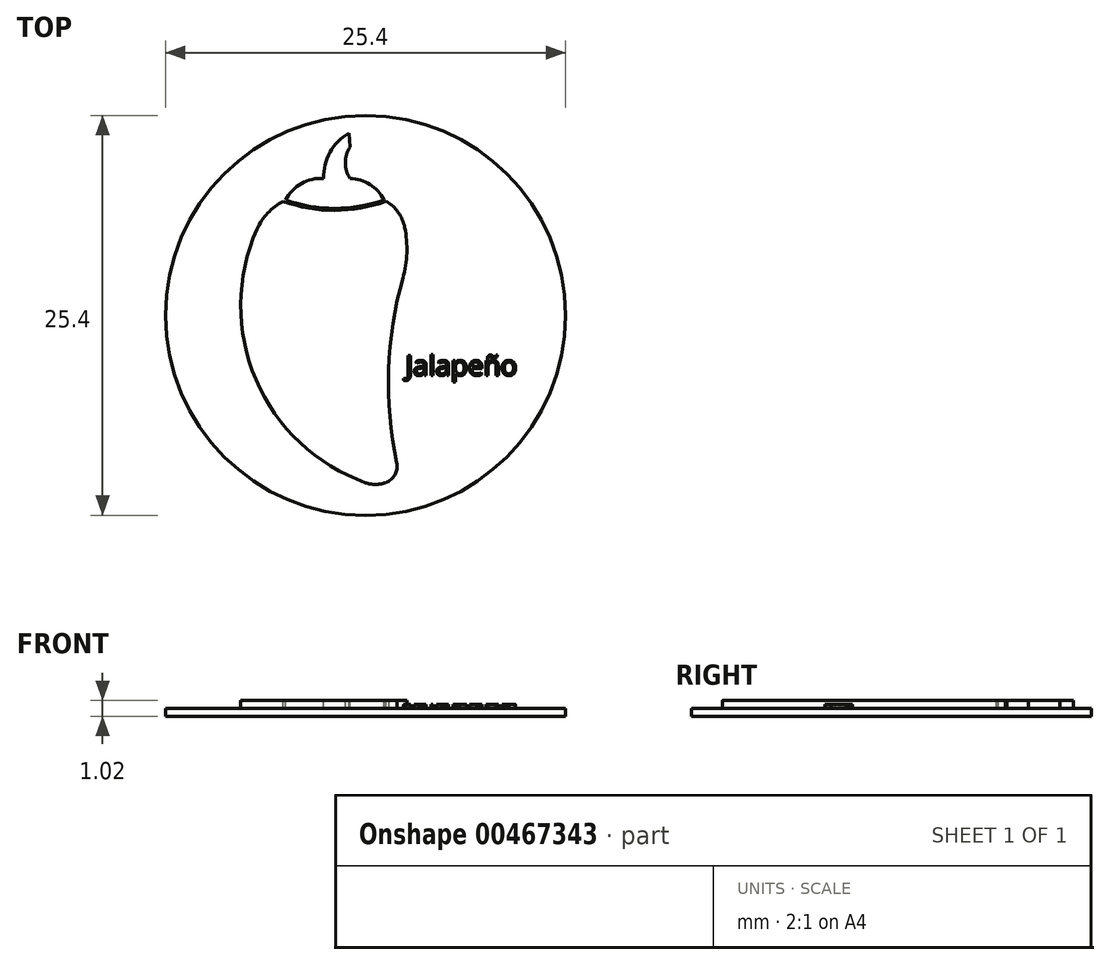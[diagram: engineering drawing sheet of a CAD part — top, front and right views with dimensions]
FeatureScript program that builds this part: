
annotation { "Feature Type Name" : "Feature", "Feature Type Description" : "" }
export const myFeature = defineFeature(function(context is Context, id is Id, definition is map)
    precondition{}
    {
        {
            var Q0;
            Q0=qCreatedBy(makeId("Top.planeOp"),FACE);
            var sketch = newSketch(context, id + "F0", { "sketchPlane" : qUnion([Q0])});
            skCircle(sketch, "E0", {"center": v(0, 0) * mm, "radius": 12.7 * mm});
            skSolve(sketch);
        }
        {
            var Q0;
            Q0=qSketchRegion(id+"F0",true);
            extrude(context, id + "F1", {"entities" : qUnion([Q0]), "depth" : 0.5 * mm});
        }
        {
            var Q0;
            Q0=makeQuery(id+"F1.opExtrude","CAP_FACE",FACE,{"disambiguationData":[OSD([sQuery(id+"F0.wireOp",EDGE,"E0")])],"isStart":false});
            var sketch = newSketch(context, id + "F2", { "sketchPlane" : qUnion([Q0])});
            skArc(sketch, "E1", {"start": v(-6.9, 5.47) * mm, "mid": v(-6.96, -4.08) * mm, "end": v(0, -10.63) * mm});
            skArc(sketch, "E2", {"start": v(-4.06, 7.62) * mm, "mid": v(-5.75, 6.91) * mm, "end": v(-6.9, 5.47) * mm});
            skLineSegment(sketch, "E3", {"start": v(-4.06, 7.62) * mm, "end": v(0, 7.62) * mm});
            skArc(sketch, "E4", {"start": v(2.5, 5.58) * mm, "mid": v(1.6, 7.04) * mm, "end": v(0, 7.62) * mm});
            skArc(sketch, "E5", {"start": v(2.37, 2.37) * mm, "mid": v(2.62, 3.97) * mm, "end": v(2.5, 5.58) * mm});
            skArc(sketch, "E6", {"start": v(2.37, 2.37) * mm, "mid": v(1.46, -3.46) * mm, "end": v(1.98, -9.34) * mm});
            skArc(sketch, "E7", {"start": v(0, -10.63) * mm, "mid": v(0.63, -10.74) * mm, "end": v(1.26, -10.63) * mm});
            skArc(sketch, "E8", {"start": v(1.26, -10.63) * mm, "mid": v(1.86, -10.12) * mm, "end": v(1.98, -9.34) * mm});
            skSolve(sketch);
        }
        {
            var Q0;
            Q0=qSketchRegion(id+"F2",true);
            extrude(context, id + "F3", {"entities" : qUnion([Q0]), "operationType" : NewBodyOperationType.ADD, "depth" : 0.5 * mm});
        }
        {
            var Q0;
            Q0=makeQuery(id+"F3.opExtrude","CAP_FACE",FACE,{"disambiguationData":[OSD([sQuery(id+"F2.wireOp",EDGE,"rHpSWnct-oIHD-Ffkf-CAhZ-aCKYbtZOLSTS"),sQuery(id+"F2.wireOp",EDGE,"E1"),sQuery(id+"F2.wireOp",EDGE,"E2"),sQuery(id+"F2.wireOp",EDGE,"E3"),sQuery(id+"F2.wireOp",EDGE,"E4"),sQuery(id+"F2.wireOp",EDGE,"E5"),sQuery(id+"F2.wireOp",EDGE,"E6"),sQuery(id+"F2.wireOp",EDGE,"QFUSNIFy-5spv-srFy-gQgj-surZsjebnAI0")])],"isStart":false});
            var sketch = newSketch(context, id + "F4", { "sketchPlane" : qUnion([Q0])});
            skArc(sketch, "E9", {"start": v(-2.65, 8.69) * mm, "mid": v(-4.07, 8.39) * mm, "end": v(-5.07, 7.32) * mm});
            skArc(sketch, "E10", {"start": v(-1.04, 11.57) * mm, "mid": v(-2.26, 10.36) * mm, "end": v(-2.65, 8.69) * mm});
            skArc(sketch, "E11", {"start": v(-0.98, 10.7) * mm, "mid": v(-1.28, 9.7) * mm, "end": v(-0.98, 8.69) * mm});
            skArc(sketch, "E12", {"start": v(1.16, 7.34) * mm, "mid": v(0.28, 8.32) * mm, "end": v(-0.98, 8.69) * mm});
            skArc(sketch, "E13", {"start": v(-5.07, 7.32) * mm, "mid": v(-1.95, 7.04) * mm, "end": v(1.16, 7.34) * mm});
            skLineSegment(sketch, "E14", {"start": v(-1.04, 11.57) * mm, "end": v(-0.98, 10.7) * mm});
            skSolve(sketch);
        }
        {
            var Q0;
            Q0=qSketchRegion(id+"F4",true);
            extrude(context, id + "F5", {"entities" : qUnion([Q0]), "operationType" : NewBodyOperationType.ADD, "oppositeDirection" : true, "depth" : 0.5 * mm});
        }
        {
            var Q0;
            Q0=makeQuery(id+"F5.boolean.opBoolean","MERGE",FACE,{"derivedFrom":[makeQuery(id+"F3.opExtrude","CAP_FACE",FACE,{"disambiguationData":[OSD([sQuery(id+"F2.wireOp",EDGE,"rHpSWnct-oIHD-Ffkf-CAhZ-aCKYbtZOLSTS"),sQuery(id+"F2.wireOp",EDGE,"E1"),sQuery(id+"F2.wireOp",EDGE,"E2"),sQuery(id+"F2.wireOp",EDGE,"E3"),sQuery(id+"F2.wireOp",EDGE,"E4"),sQuery(id+"F2.wireOp",EDGE,"E5"),sQuery(id+"F2.wireOp",EDGE,"E6"),sQuery(id+"F2.wireOp",EDGE,"QFUSNIFy-5spv-srFy-gQgj-surZsjebnAI0")])],"isStart":false}),makeQuery(id+"F5.opExtrude","CAP_FACE",FACE,{"disambiguationData":[OSD([sQuery(id+"F4.wireOp",EDGE,"E9"),sQuery(id+"F4.wireOp",EDGE,"E10"),sQuery(id+"F4.wireOp",EDGE,"e30zH5Q7-4QPd-AqFn-v8pD-EV9Xd4VOZ2Ve"),sQuery(id+"F4.wireOp",EDGE,"RqdcVehB-sg3L-RL1e-PxLt-mhJ17zwqFt0n"),sQuery(id+"F4.wireOp",EDGE,"E11"),sQuery(id+"F4.wireOp",EDGE,"E12"),sQuery(id+"F4.wireOp",EDGE,"E13")])],"isStart":true})]});
            var sketch = newSketch(context, id + "F6", { "sketchPlane" : qUnion([Q0])});
            skArc(sketch, "E15", {"start": v(-5.07, 7.32) * mm, "mid": v(-1.95, 6.8) * mm, "end": v(1.16, 7.34) * mm});
            skArc(sketch, "E16", {"start": v(-5.23, 7.25) * mm, "mid": v(-1.96, 6.67) * mm, "end": v(1.31, 7.26) * mm});
            skArc(sketch, "E17", {"start": v(-5.07, 7.32) * mm, "mid": v(-5.15, 7.29) * mm, "end": v(-5.23, 7.25) * mm});
            skArc(sketch, "E18", {"start": v(1.31, 7.26) * mm, "mid": v(1.24, 7.3) * mm, "end": v(1.16, 7.34) * mm});
            skSolve(sketch);
        }
        {
            var Q0;
            Q0=qSketchRegion(id+"F6",true);
            extrude(context, id + "F7", {"entities" : qUnion([Q0]), "operationType" : NewBodyOperationType.REMOVE, "oppositeDirection" : true, "depth" : 0.5 * mm});
        }
        {
            var Q0;
            Q0=makeQuery(id+"F7.boolean.opBoolean","MERGE",FACE,{"derivedFrom":[makeQuery(id+"F1.opExtrude","CAP_FACE",FACE,{"disambiguationData":[OSD([sQuery(id+"F0.wireOp",EDGE,"E0")])],"isStart":false}),makeQuery(id+"F7.opExtrude","CAP_FACE",FACE,{"disambiguationData":[OSD([sQuery(id+"F6.wireOp",EDGE,"E15"),sQuery(id+"F6.wireOp",EDGE,"E16"),sQuery(id+"F6.wireOp",EDGE,"E17"),sQuery(id+"F6.wireOp",EDGE,"E18")])],"isStart":false})]});
            var sketch = newSketch(context, id + "F8", { "sketchPlane" : qUnion([Q0])});
            skText(sketch, "E19", { "text": "Jalapeño", "fontName": "OpenSans-Regular.ttf"});
            const initialGuessF8  = {"E19": [0.00254, -0.00381, 1, 0, 0.00127]};
            skSetInitialGuess(sketch, initialGuessF8);
            skSolve(sketch);
        }
        {
            var Q0;
            Q0 = qSketchRegion(id + "F8", true);
            extrude(context, id + "F9", {"entities" : qUnion([Q0]), "operationType" : NewBodyOperationType.ADD, "depth" : 0.25 * mm});
        }
    });
